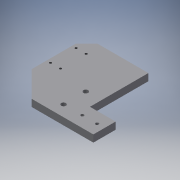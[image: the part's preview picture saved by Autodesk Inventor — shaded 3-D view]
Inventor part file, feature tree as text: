
AUTODESK INVENTOR PART (.ipt)
format: ipt  version: 2018 (Build 220112000, 112)  size: 146,944 bytes
history: native  units: mm
features: sketch x4, hole x3, other x1, extrude x1, chamfer x1
ambient origin geometry x8: Origin, YZ Plane, XZ Plane, XY Plane, X Axis, Y Axis, Z Axis, Center Point
bodies: Body1 (feature_tree)
feature tree (10):
  other  "Sólido1"
  extrude  "Extrusão1"  Depth=40.0mm
  chamfer  "Chanfro1"  Distance=12.7mm
  hole  "Furo1"  [1 undecoded]
  hole  "Furo2"  [1 undecoded]
  hole  "Furo3"  [1 undecoded]
  sketch  "Esboço1"  dims[d0=111.0mm d5=40.0mm]
  sketch  "Esboço2"  dims[d6=105.0mm]
  sketch  "Esboço3"  dims[d7=135.0deg]
  sketch  "Esboço4"  dims[d8=98.71536mm d9=12.7mm d10=0.0mm d11=157.066236mm d12=20.0mm d13=2.0mm d14=45.0deg d15=4.134mm d16=10.0mm d17=4.0mm d18=2.0mm d19=90.0deg d20=14.2mm d21=20.594885mm d22=27.5mm d23=27.5mm d24=60.0mm d25=20.0mm d26=8.5mm d27=10.0mm d28=4.0mm d29=2.0mm d30=90.0deg d31=14.2mm d32=20.594885mm d33=13.25mm d34=39.75mm d35=20.0mm d36=20.0mm d37=5.5mm d38=10.0mm d39=4.0mm d40=2.0mm d41=90.0deg d42=14.2mm d43=20.594885mm]
note: 3 required parameter values undecoded (feature->parameter linkage not recoverable at this tier; creation-order binding heuristic only, values carry confidence <= 0.55)
